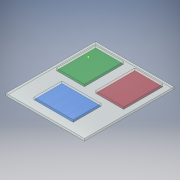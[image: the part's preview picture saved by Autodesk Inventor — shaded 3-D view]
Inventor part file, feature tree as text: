
AUTODESK INVENTOR PART (.ipt)
format: ipt  version: 2018 (Build 220112000, 112)  size: 135,680 bytes
history: native  units: in
note: dims shown in document units (in); Inventor stores cm internally (conversion verified against a paired STEP export)
features: sketch x3, extrude x2
ambient origin geometry x8: Origin, YZ Plane, XZ Plane, XY Plane, X Axis, Y Axis, Z Axis, Center Point
bodies: Solid1 (feature_tree)
feature tree (5):
  extrude  "Extrusion1"  Depth=5.5118in
  sketch  "Sketch2"  dims[d2=0.1575in d3=0.0in d4=1.9685in]
  extrude  "Extrusion2"  Depth=1.9685in
  sketch  "Sketch1"  dims[d0=6.2992in d1=5.5118in]
  sketch  "Sketch3"  dims[d5=2.7559in d6=1.9685in d7=1.9685in d8=2.7559in d9=2.7559in d10=0.5906in d11=0.3937in d12=0.3937in d13=0.3937in d14=0.3937in d15=1.378in d16=1.378in d17=0.1575in d18=0.0in]
